# Revit family: Haworth_JiveTable_HalfPebbleBases
name_source: partatom
category: Furniture Systems
revit_build: Autodesk Revit 2018 (Build: 20170223_1515(x64)
units: mm (PartAtom-declared; Revit-internal decimal feet)

## family parameters
Always vertical = Yes
Cut with Voids When Loaded = No
OmniClass Number = 23.40.70.14.64.21
OmniClass Title = Systems Furniture
Part Type = Normal
Room Calculation Point = No
Round Connector Dimension = Use Diameter
Shared = No
Work Plane-Based = No

## types (11) — shared parameters
Assembly Code = E2020200
Casters = No
Glides = Yes
Manufacturer = Haworth, Inc.
Max. Depth = 60"
Max. Height = 42"
Max. Width = 60"
Min. Depth = 42"
Min. Height = 29"
Min. Width = 42"
Model = Haworth Jive
Revision Number = 0
Size = Verify Final Dim. w/ Haworth
Standard Depths = 42, 48, 54, 60 in.
Standard Heights = 29, 42 in.
Standard Widths = 42, 48, 54, 60 in.
Table Thickness = 1 3/16"
URL = http://www.haworth.com
URL - Product = http://www.haworth.com
Warranty = http://www.haworth.com

## per-type parameters (varying)
| type | 2 Column | 4 Column | Actual Depth | Actual Height | Actual Width | Base Center | Close Legs | Custom Size | Depth | Description | Far Legs | Height | Leg Height | Table Radius | Vert. Leg Center | Width |
| 42d 42w 29h - Bridge Base - With Casters | Yes | No | 42" | 29" | 42" | 20" | 7" | No | 42" | Haworth Jive Table Half Pebble Bases - 42d 42w 29h - Bridge Base - With Casters | 31" | 29" | 27 13/16" | 21" | 11" | 42" |
| 42d 42w 29h - Bridge Base - With Glides | Yes | No | 42" | 29" | 42" | 20" | 7" | No | 42" | Haworth Jive Table Half Pebble Bases - 42d 42w 29h - Bridge Base - With Glides | 31" | 29" | 27 13/16" | 21" | 11" | 42" |
| 42d 42w 42h - Bridge Base - With Casters | Yes | No | 42" | 42" | 42" | 20" | 7" | Yes | 42" | Haworth Jive Table Half Pebble Bases - 42d 42w 42h - Bridge Base - With Casters | 31" | 42" | 40 13/16" | 21" | 11" | 42" |
| 42d 42w 42h - Bridge Base - With Glides | Yes | No | 42" | 42" | 42" | 20" | 7" | Yes | 42" | Haworth Jive Table Half Pebble Bases - 42d 42w 42h - Bridge Base - With Glides | 31" | 42" | 40 13/16" | 21" | 11" | 42" |
| 48d 48w 29h - Bridge Base - With Casters | Yes | No | 48" | 29" | 48" | 23" | 8" | No | 48" | Haworth Jive Table Half Pebble Bases - 48d 48w 29h - Bridge Base - With Casters | 36" | 29" | 27 13/16" | 24" | 15" | 48" |
| 48d 48w 29h - Bridge Base - With Glides | Yes | No | 48" | 29" | 48" | 23" | 8" | No | 48" | Haworth Jive Table Half Pebble Bases - 48d 48w 29h - Bridge Base - With Glides | 36" | 29" | 27 13/16" | 24" | 15" | 48" |
| 48d 48w 42h - Bridge Base - With Casters | Yes | No | 48" | 42" | 48" | 23" | 8" | Yes | 48" | Haworth Jive Table Half Pebble Bases - 48d 48w 42h - Bridge Base - With Casters | 36" | 42" | 40 13/16" | 24" | 15" | 48" |
| 48d 48w 42h - Bridge Base - With Glides | Yes | No | 48" | 42" | 48" | 23" | 8" | Yes | 48" | Haworth Jive Table Half Pebble Bases - 48d 48w 42h - Bridge Base - With Glides | 36" | 42" | 40 13/16" | 24" | 15" | 48" |
| 54d 54w 29h - Bridge Base - With Glides | No | Yes | 54" | 29" | 54" | 26" | 10" | No | 54" | Haworth Jive Table Half Pebble Bases - 54d 54w 29h - Bridge Base - With Glides | 41" | 29" | 27 13/16" | 27" | 17" | 54" |
| 54d 54w 42h - Bridge Base - With Glides | No | Yes | 54" | 42" | 54" | 26" | 10" | Yes | 54" | Haworth Jive Table Half Pebble Bases - 54d 54w 42h - Bridge Base - With Glides | 41" | 42" | 40 13/16" | 27" | 17" | 54" |
| 60d 60w 29h - Bridge Base - With Glides | No | Yes | 60" | 29" | 60" | 29" | 11" | No | 60" | Haworth Jive Table Half Pebble Bases - 60d 60w 29h - Bridge Base - With Glides | 45" | 29" | 27 13/16" | 30" | 19" | 60" |

## geometry (parser evidence)
native form markers: Sweep x30
no freeform markers — native parametric forms only
